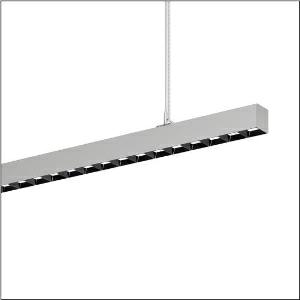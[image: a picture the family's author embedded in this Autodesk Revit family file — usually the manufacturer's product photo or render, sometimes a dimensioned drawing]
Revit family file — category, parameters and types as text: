
# Revit family: silica_r__21_51mx31dc4dsb_9913
name_source: partatom
category: Lighting Fixtures
units: mm (PartAtom-declared; Revit-internal decimal feet)

## family parameters
Cut with Voids When Loaded = No
Host = Face
Light Source = No
Part Type = Normal
Room Calculation Point = No
Round Connector Dimension = Use Diameter
Shared = No

## types (1)
- --- (1 x LED, 18230 lm, 105.9 W, 4000K)
    Apparent Load = 106 VA
    CIE Flux Codes = 87 99 100 59 100
    Color Rendering = 80
    Color Temperature = 4000K
    Default Elevation = 1800 mm
    Description = Silica® 21, office luminaire, primary light control with darklight reflector, of PMMA, black, CAT 2 (L<= 3000cd/m²), light emission: direct/indirect distribution, primary light characteristic: symmetric, installation type: suspended mounting, LED, rated luminous flux: 18.230lm, luminous efficacy: 172lm/W, light colour: 840, colour temperature: 4000K, with terminal, 3+2-pole, max. 2.5mm², mains connection: 220..240V, AC, 50/60Hz, rated input power: 105.9W, luminaire housing, of aluminium, metallic grey (RAL 9006), length: 3.004mm, width: 53mm, height: 53mm, protection rating (complete): IP20, insulation class (complete): insulation class I (protective earthing), certification: CE, permissible operating ambient temperature: 0..+35°C, standard: EN 50419, packaging unit: 1 piece
    Height = 53 mm
    Lamp = 1 x LED
    Lamp Light Flux = 18230 lm
    Lamp Power = 105.9 W
    Lamp count = 1
    Length = 3004 mm
    Luminous efficacy = 172 lm/W
    Manufacturer = Siteco
    ModVariant = No
    Model = 51MX31DC4DSB
    Mounting Place = Ceiling
    Mounting Type = Pendant
    Number of Poles = 1
    OnlyDefault = Yes
    Power Factor = 1
    Product Name = Silica® 21
    Product group = office luminaire | ceiling pendant
    ProductGroupID = 902
    Protection Class = Protection class I
    Protection Degree = IP 20
    RLX_Detail_Level = 1
    RLX_Emergency_Light_Flux = 0 lm
    RLX_Emergency_Type = 0
    RLX_Emergency_Type_DB = No
    RlxData = <blob elided: 66205 chars, md5=8195b761>
    Socket = socket
    Standby Power = 0 W
    System Light Flux = 18230 lm
    System Power = 106 W
    Type Comments = factory setting: luminous flux: 100 % | dim-lin: 254 | 367 mA
    Type Image = l_1335859.jpg
    URL = http://relux.com
    VarID = @adj_090479
    Voltage = 0 V
    Weight = 0.00 kg
    Width = 53 mm

## geometry (parser evidence)
native form markers: Blend x4, Sweep x10
no freeform markers — native parametric forms only
